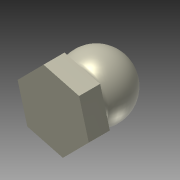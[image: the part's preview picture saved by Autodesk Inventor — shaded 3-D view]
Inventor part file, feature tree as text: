
AUTODESK INVENTOR PART (.ipt)
format: ipt  version: 2012 (Build 160160000, 160)  size: 124,928 bytes
history: native  units: mm
features: sketch x2, revolve x1, extrude x1, fillet x1
ambient origin geometry x8: Origin, YZ Plane, XZ Plane, XY Plane, X Axis, Y Axis, Z Axis, Center Point
bodies: Solid1 (feature_tree)
feature tree (5):
  revolve  "Revolution1"  [1 undecoded]
  extrude  "Extrusion1"  Depth=7.0mm
  fillet  "Fillet1"  Radius=2.0mm
  sketch  "Sketch1"  dims[d0=7.0mm d1=4.0mm]
  sketch  "Sketch2"  dims[d2=90.0deg d3=7.0mm d4=2.0mm d5=0.0mm d6=0.5mm]
note: 1 required parameter value undecoded (feature->parameter linkage not recoverable at this tier; creation-order binding heuristic only, values carry confidence <= 0.55)
